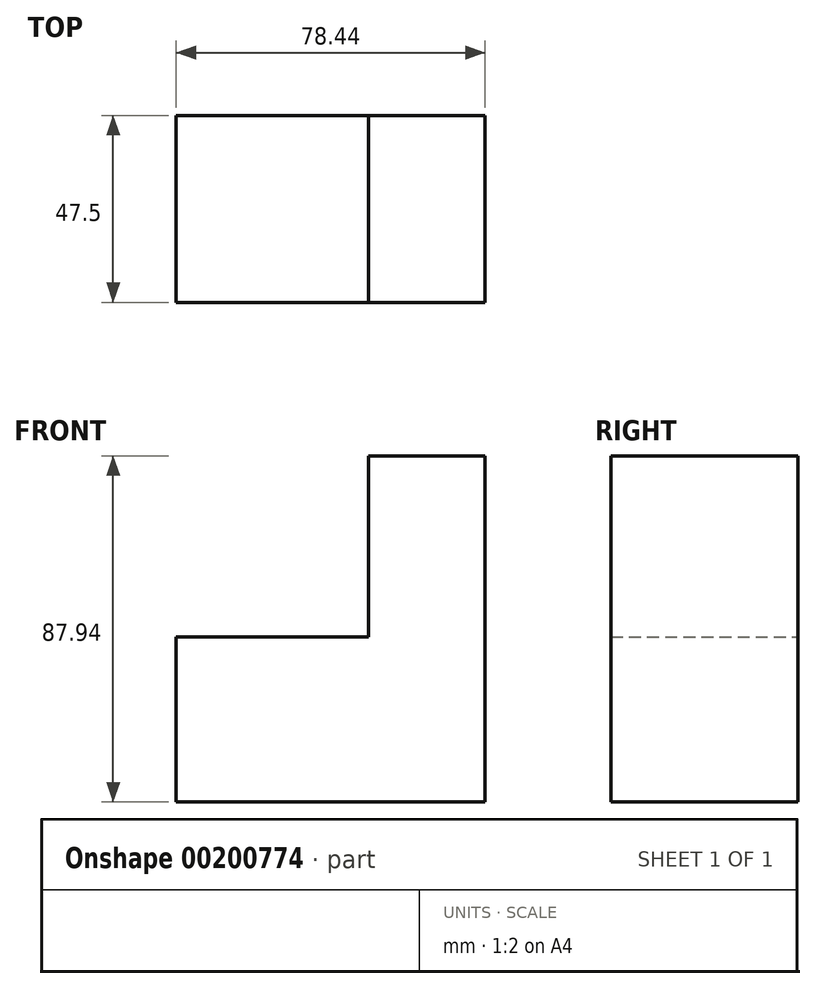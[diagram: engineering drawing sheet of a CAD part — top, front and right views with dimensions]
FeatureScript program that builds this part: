
annotation { "Feature Type Name" : "Feature", "Feature Type Description" : "" }
export const myFeature = defineFeature(function(context is Context, id is Id, definition is map)
    precondition{}
    {
        {
            var Q0;
            Q0=qCreatedBy(makeId("Front.planeOp"),FACE);
            var sketch = newSketch(context, id + "F0", { "sketchPlane" : qUnion([Q0])});
            skLineSegment(sketch, "E0", {"start": v(-33.63, 18.67) * mm, "end": v(15.17, 18.67) * mm});
            skLineSegment(sketch, "E1", {"start": v(15.17, 18.67) * mm, "end": v(15.17, 64.65) * mm});
            skLineSegment(sketch, "E2", {"start": v(15.17, 64.65) * mm, "end": v(15.17, 64.65) * mm});
            skLineSegment(sketch, "E3", {"start": v(15.17, 64.65) * mm, "end": v(44.8, 64.65) * mm});
            skLineSegment(sketch, "E4", {"start": v(44.8, 64.65) * mm, "end": v(44.8, -23.3) * mm});
            skLineSegment(sketch, "E5", {"start": v(44.8, -23.3) * mm, "end": v(-33.63, -23.3) * mm});
            skLineSegment(sketch, "E6", {"start": v(-33.63, -23.3) * mm, "end": v(-33.63, 18.67) * mm});
            skSolve(sketch);
        }
        {
            var Q0;
            Q0=makeQuery(id+"F0.imprint","IMPRINT",FACE,{"disambiguationData":[TD([[makeQuery(id+"F0.imprint","IMPRINT",EDGE,{"derivedFrom":sQuery(id+"F0.wireOp",EDGE,"E0")}),-1.0]])]});
            extrude(context, id + "F1", {"entities" : qUnion([Q0]), "depth" : 47.5 * mm});
        }
    });
